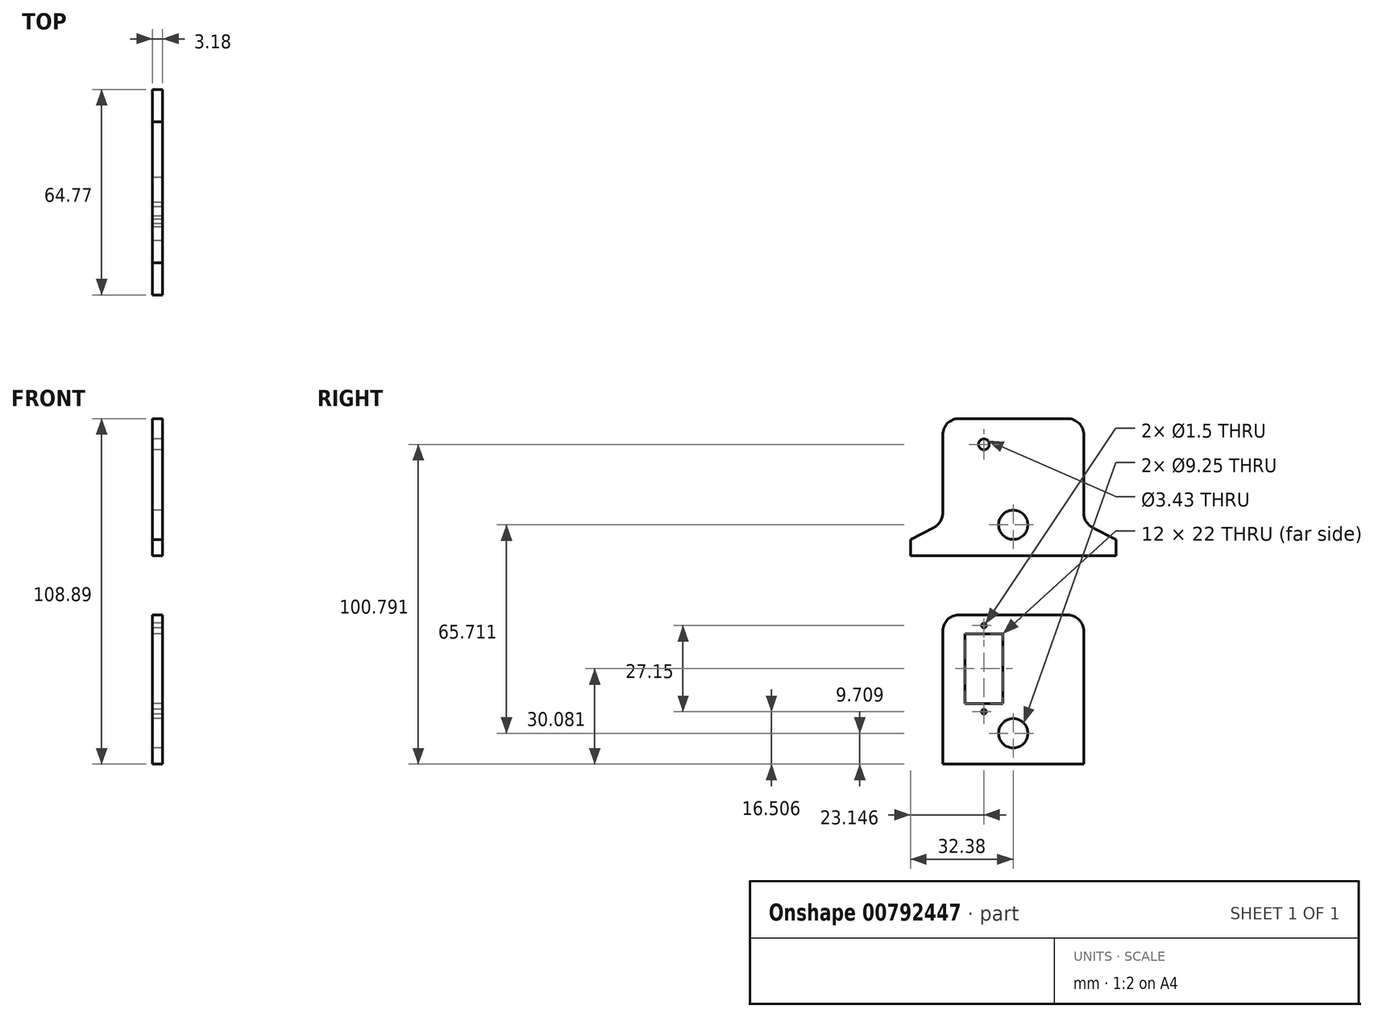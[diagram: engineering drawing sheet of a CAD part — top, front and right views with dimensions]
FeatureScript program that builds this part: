
annotation { "Feature Type Name" : "Feature", "Feature Type Description" : "" }
export const myFeature = defineFeature(function(context is Context, id is Id, definition is map)
    precondition{}
    {
        {
            var Q0;
            Q0=qCreatedBy(makeId("Right.planeOp"),FACE);
            var sketch = newSketch(context, id + "F0", { "sketchPlane" : qUnion([Q0])});
            skLineSegment(sketch, "E0.bottom", {"start": v(-72.3, -44.44) * mm, "end": v(-27.85, -44.44) * mm});
            skLineSegment(sketch, "E0.top", {"start": v(-72.3, 2.55) * mm, "end": v(-27.85, 2.55) * mm});
            skLineSegment(sketch, "E0.left", {"start": v(-72.3, -44.44) * mm, "end": v(-72.3, 2.55) * mm});
            skLineSegment(sketch, "E0.right", {"start": v(-27.85, -44.44) * mm, "end": v(-27.85, 2.55) * mm});
            skLineSegment(sketch, "E1.bottom", {"start": v(-53.31, -25.36) * mm, "end": v(-65.31, -25.36) * mm});
            skLineSegment(sketch, "E1.top", {"start": v(-53.31, -3.36) * mm, "end": v(-65.31, -3.36) * mm});
            skLineSegment(sketch, "E1.left", {"start": v(-53.31, -25.36) * mm, "end": v(-53.31, -3.36) * mm});
            skLineSegment(sketch, "E1.right", {"start": v(-65.31, -25.36) * mm, "end": v(-65.31, -3.36) * mm});
            skLineSegment(sketch, "E2", {"start": v(-65.31, -3.36) * mm, "end": v(-65.31, 1.8) * mm});
            skLineSegment(sketch, "E3", {"start": v(-65.31, 1.8) * mm, "end": v(-53.31, 1.8) * mm});
            skLineSegment(sketch, "E4", {"start": v(-53.31, 1.8) * mm, "end": v(-53.31, -3.36) * mm});
            skLineSegment(sketch, "E5", {"start": v(-53.31, -25.36) * mm, "end": v(-53.31, -30.5) * mm});
            skLineSegment(sketch, "E6", {"start": v(-53.31, -30.5) * mm, "end": v(-65.31, -30.5) * mm});
            skLineSegment(sketch, "E7", {"start": v(-65.31, -30.5) * mm, "end": v(-65.31, -25.36) * mm});
            skCircle(sketch, "E8", {"center": v(-59.31, -9.36) * mm, "radius": 6 * mm});
            skPoint(sketch, "E8.centerSnap0", {"position": v(-59.31, -3.36) * mm});
            skArc(sketch, "E9", {"start": v(-61.62, -14.9) * mm, "mid": v(-59.31, -18.36) * mm, "end": v(-57, -14.9) * mm});
            skCircle(sketch, "E10", {"center": v(-59.31, -0.78) * mm, "radius": 0.75 * mm});
            skPoint(sketch, "E10.centerSnap0", {"position": v(-65.31, -0.78) * mm});
            skPoint(sketch, "E10.centerSnap1", {"position": v(-59.31, 1.8) * mm});
            skCircle(sketch, "E11", {"center": v(-59.31, -27.93) * mm, "radius": 0.75 * mm});
            skPoint(sketch, "E11.centerSnap0", {"position": v(-59.31, -25.36) * mm});
            skPoint(sketch, "E11.centerSnap1", {"position": v(-65.31, -27.93) * mm});
            skCircle(sketch, "E12", {"center": v(-59.31, -9.36) * mm, "radius": 2.25 * mm});
            skPoint(sketch, "E13", {"position": v(-50.08, 2.55) * mm});
            skPoint(sketch, "E14", {"position": v(-50.08, -44.44) * mm});
            skCircle(sketch, "E15", {"center": v(-50.08, -34.73) * mm, "radius": 4.62 * mm});
            skLineSegment(sketch, "E16", {"start": v(-50.08, 2.55) * mm, "end": v(-50.08, -44.44) * mm, "construction": true});
            skLineSegment(sketch, "E17", {"start": v(-59.31, -9.36) * mm, "end": v(-50.08, -34.73) * mm, "construction": true});
            skLineSegment(sketch, "E18.bottom", {"start": v(-72.3, 21.27) * mm, "end": v(-27.85, 21.27) * mm});
            skLineSegment(sketch, "E18.top", {"start": v(-61.38, 64.45) * mm, "end": v(-59.6, 64.45) * mm});
            skLineSegment(sketch, "E18.left", {"start": v(-72.3, 21.27) * mm, "end": v(-72.3, 64.45) * mm});
            skLineSegment(sketch, "E19.bottom", {"start": v(-53.31, 40.35) * mm, "end": v(-65.31, 40.35) * mm, "construction": true});
            skLineSegment(sketch, "E19.top", {"start": v(-53.31, 62.35) * mm, "end": v(-65.31, 62.35) * mm, "construction": true});
            skLineSegment(sketch, "E19.left", {"start": v(-53.31, 40.35) * mm, "end": v(-53.31, 62.35) * mm, "construction": true});
            skLineSegment(sketch, "E19.right", {"start": v(-65.31, 40.35) * mm, "end": v(-65.31, 62.35) * mm, "construction": true});
            skLineSegment(sketch, "E20", {"start": v(-65.31, 62.35) * mm, "end": v(-65.31, 67.5) * mm, "construction": true});
            skLineSegment(sketch, "E21", {"start": v(-65.31, 67.5) * mm, "end": v(-53.31, 67.5) * mm, "construction": true});
            skLineSegment(sketch, "E22", {"start": v(-53.31, 67.5) * mm, "end": v(-53.31, 62.35) * mm, "construction": true});
            skLineSegment(sketch, "E23", {"start": v(-53.31, 40.35) * mm, "end": v(-53.31, 35.2) * mm, "construction": true});
            skLineSegment(sketch, "E24", {"start": v(-53.31, 35.2) * mm, "end": v(-65.31, 35.2) * mm, "construction": true});
            skLineSegment(sketch, "E25", {"start": v(-65.31, 35.2) * mm, "end": v(-65.31, 40.35) * mm, "construction": true});
            skCircle(sketch, "E26", {"center": v(-59.31, 56.35) * mm, "radius": 6 * mm, "construction": true});
            skPoint(sketch, "E26.centerSnap0", {"position": v(-59.31, 62.35) * mm});
            skArc(sketch, "E27", {"start": v(-61.62, 50.81) * mm, "mid": v(-59.31, 47.35) * mm, "end": v(-57, 50.81) * mm, "construction": true});
            skCircle(sketch, "E28", {"center": v(-59.31, 64.93) * mm, "radius": 0.75 * mm, "construction": true});
            skPoint(sketch, "E28.centerSnap0", {"position": v(-65.31, 64.93) * mm});
            skPoint(sketch, "E28.centerSnap1", {"position": v(-59.31, 67.5) * mm});
            skCircle(sketch, "E29", {"center": v(-59.31, 37.78) * mm, "radius": 0.75 * mm, "construction": true});
            skPoint(sketch, "E29.centerSnap0", {"position": v(-59.31, 40.35) * mm});
            skPoint(sketch, "E29.centerSnap1", {"position": v(-65.31, 37.78) * mm});
            skCircle(sketch, "E30", {"center": v(-59.31, 56.35) * mm, "radius": 2.25 * mm, "construction": true});
            skPoint(sketch, "E31", {"position": v(-50.08, 64.45) * mm});
            skPoint(sketch, "E32", {"position": v(-50.08, 21.27) * mm});
            skCircle(sketch, "E33", {"center": v(-50.08, 30.98) * mm, "radius": 4.62 * mm});
            skLineSegment(sketch, "E34", {"start": v(-50.08, 64.45) * mm, "end": v(-50.08, 21.27) * mm, "construction": true});
            skLineSegment(sketch, "E35", {"start": v(-59.31, 56.35) * mm, "end": v(-50.08, 30.98) * mm, "construction": true});
            skCircle(sketch, "E36", {"center": v(-59.31, 56.35) * mm, "radius": 1.71 * mm});
            skPoint(sketch, "E37.visualSharp", {"position": v(-72.3, 64.45) * mm});
            skPoint(sketch, "E38.visualSharp", {"position": v(-54.52, 64.45) * mm});
            skLineSegment(sketch, "E39", {"start": v(-72.3, 64.45) * mm, "end": v(-27.85, 64.45) * mm});
            skLineSegment(sketch, "E40", {"start": v(-27.85, 64.45) * mm, "end": v(-27.85, 21.27) * mm});
            skLineSegment(sketch, "E41", {"start": v(-27.85, 21.27) * mm, "end": v(-17.7, 21.27) * mm});
            skLineSegment(sketch, "E42", {"start": v(-72.3, 21.27) * mm, "end": v(-82.46, 21.27) * mm});
            skLineSegment(sketch, "E43", {"start": v(-17.7, 21.27) * mm, "end": v(-17.7, 26.35) * mm});
            skLineSegment(sketch, "E44", {"start": v(-17.7, 26.35) * mm, "end": v(-27.85, 31.6) * mm});
            skLineSegment(sketch, "E45", {"start": v(-82.46, 21.27) * mm, "end": v(-82.46, 26.35) * mm});
            skLineSegment(sketch, "E46", {"start": v(-82.46, 26.35) * mm, "end": v(-72.3, 31.6) * mm});
            skSolve(sketch);
        }
        {
            var Q0;
            Q0=makeQuery(id+"F0.imprint","IMPRINT",FACE,{"disambiguationData":[TD([[makeQuery(id+"F0.imprint","IMPRINT",EDGE,{"derivedFrom":sQuery(id+"F0.wireOp",EDGE,"E18.bottom")}),1.0]])]});
            var Q1;
            Q1=makeQuery(id+"F0.imprint","IMPRINT",FACE,{"disambiguationData":[TD([[makeQuery(id+"F0.imprint","IMPRINT",EDGE,{"derivedFrom":sQuery(id+"F0.wireOp",EDGE,"1f746809-ccef-4b12-823a-4d46f3119de00.MirrorC")}),1.0]])]});
            var Q2;
            Q2=makeQuery(id+"F0.imprint","IMPRINT",FACE,{"disambiguationData":[TD([[makeQuery(id+"F0.imprint","IMPRINT",EDGE,{"derivedFrom":sQuery(id+"F0.wireOp",EDGE,"E0.bottom")}),1.0]])]});
            var Q3;
            {var subQ0=sQuery(id+"F0.wireOp",EDGE,"E2");Q3=makeQuery(id+"F0.imprint","IMPRINT",FACE,{"disambiguationData":[TD([[makeQuery(id+"F0.imprint","IMPRINT",EDGE,{"derivedFrom":subQ0}),-1.0]])]});}
            var Q4;
            Q4=makeQuery(id+"F0.imprint","IMPRINT",FACE,{"disambiguationData":[TD([[makeQuery(id+"F0.imprint","IMPRINT",EDGE,{"derivedFrom":sQuery(id+"F0.wireOp",EDGE,"E1.bottom")}),1.0]])]});
            var Q5;
            Q5=makeQuery(id+"F0.imprint","IMPRINT",FACE,{"disambiguationData":[TD([[makeQuery(id+"F0.imprint","IMPRINT",EDGE,{"derivedFrom":sQuery(id+"F0.wireOp",EDGE,"1f746809-ccef-4b12-823a-4d46f3119de06.MirrorCS")}),-1.0]])]});
            var Q6;
            Q6=makeQuery(id+"F0.imprint","IMPRINT",FACE,{"disambiguationData":[TD([[makeQuery(id+"F0.imprint","IMPRINT",EDGE,{"derivedFrom":sQuery(id+"F0.wireOp",EDGE,"1f746809-ccef-4b12-823a-4d46f3119de06.MirrorCS")}),1.0]])]});
            var Q7;
            Q7=makeQuery(id+"F0.imprint","IMPRINT",FACE,{"disambiguationData":[TD([[makeQuery(id+"F0.imprint","IMPRINT",EDGE,{"derivedFrom":sQuery(id+"F0.wireOp",EDGE,"1f746809-ccef-4b12-823a-4d46f3119de07.MirrorCS")}),1.0]])]});
            var Q8;
            {var subQ0=sQuery(id+"F0.wireOp",EDGE,"E42");Q8=makeQuery(id+"F0.imprint","IMPRINT",FACE,{"disambiguationData":[TD([[makeQuery(id+"F0.imprint","IMPRINT",EDGE,{"derivedFrom":subQ0}),-1.0]])]});}
            var Q9;
            {var subQ0=sQuery(id+"F0.wireOp",EDGE,"E41");Q9=makeQuery(id+"F0.imprint","IMPRINT",FACE,{"disambiguationData":[TD([[makeQuery(id+"F0.imprint","IMPRINT",EDGE,{"derivedFrom":subQ0}),1.0]])]});}
            extrude(context, id + "F1", {"entities" : qUnion([Q0, Q1, Q2, Q3, Q4, Q5, Q6, Q7, Q8, Q9]), "depth" : 3.17 * mm, "offsetDistance" : 25.4 * mm});
        }
        {
            var Q0;
            Q0=makeQuery(id+"F1.opExtrude","SWEPT_EDGE",EDGE,{"disambiguationData":[OSD([sQuery(id+"F0.wireOp",EDGE,"E39"),sQuery(id+"F0.wireOp",EDGE,"E40")])]});
            var Q1;
            Q1=makeQuery(id+"F1.opExtrude","SWEPT_EDGE",EDGE,{"disambiguationData":[OSD([sQuery(id+"F0.wireOp",EDGE,"E18.left"),sQuery(id+"F0.wireOp",EDGE,"E39")])]});
            var Q2;
            Q2=makeQuery(id+"F1.opExtrude","SWEPT_EDGE",EDGE,{"disambiguationData":[OSD([sQuery(id+"F0.wireOp",EDGE,"E0.top"),sQuery(id+"F0.wireOp",EDGE,"E0.left")])]});
            var Q3;
            Q3=makeQuery(id+"F1.opExtrude","SWEPT_EDGE",EDGE,{"disambiguationData":[OSD([sQuery(id+"F0.wireOp",EDGE,"E0.top"),sQuery(id+"F0.wireOp",EDGE,"E0.right")])]});
            var Q4;
            Q4=makeQuery(id+"F1.opExtrude","SWEPT_EDGE",EDGE,{"disambiguationData":[OSD([sQuery(id+"F0.wireOp",EDGE,"1f746809-ccef-4b12-823a-4d46f3119de034.MirrorCS"),sQuery(id+"F0.wireOp",EDGE,"1f746809-ccef-4b12-823a-4d46f3119de037.MirrorCS")])]});
            var Q5;
            Q5=makeQuery(id+"F1.opExtrude","SWEPT_EDGE",EDGE,{"disambiguationData":[OSD([sQuery(id+"F0.wireOp",EDGE,"1f746809-ccef-4b12-823a-4d46f3119de034.MirrorCS"),sQuery(id+"F0.wireOp",EDGE,"1f746809-ccef-4b12-823a-4d46f3119de049.MirrorCS")])]});
            var Q6;
            Q6=makeQuery(id+"F1.opExtrude","SWEPT_EDGE",EDGE,{"disambiguationData":[OSD([sQuery(id+"F0.wireOp",EDGE,"E40"),sQuery(id+"F0.wireOp",EDGE,"nEYrh93h-Z6Ug-uvgy-zeT3-qd8f8WGW7Sgm")])]});
            var Q7;
            Q7=makeQuery(id+"F1.opExtrude","SWEPT_EDGE",EDGE,{"disambiguationData":[OSD([sQuery(id+"F0.wireOp",EDGE,"E18.left"),sQuery(id+"F0.wireOp",EDGE,"EJYNetgp-3oaK-YG5Z-rnWC-JxbzKw0fUnP5")])]});
            fillet(context, id + "F2", {"entities" : qUnion([Q0, Q1, Q2, Q3, Q4, Q5, Q6, Q7]), "radius" : 5.08 * mm, "tangentPropagation" : true, "allowEdgeOverflow" : false});
        }
    });
